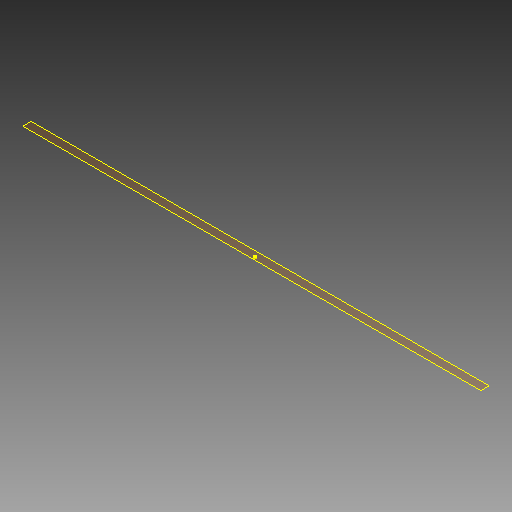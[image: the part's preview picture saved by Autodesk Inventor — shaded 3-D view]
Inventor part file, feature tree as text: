
AUTODESK INVENTOR PART (.ipt)
format: ipt  version: 2019 (Build 230136000, 136)  size: 82,944 bytes
history: native  units: mm
features: other x3, plane x1, sketch x1
ambient origin geometry x8: Origin, YZ Plane, XZ Plane, XY Plane, X Axis, Y Axis, Z Axis, Center Point
feature tree (5):
  plane  "Work Plane2"
  sketch  "Sketch3"
  other  "<userpath>\Stuff\Ajedrez2\Ajedrez2.iam"
  other  "Ajedrez2.iam"
  other  "Floor:1"
